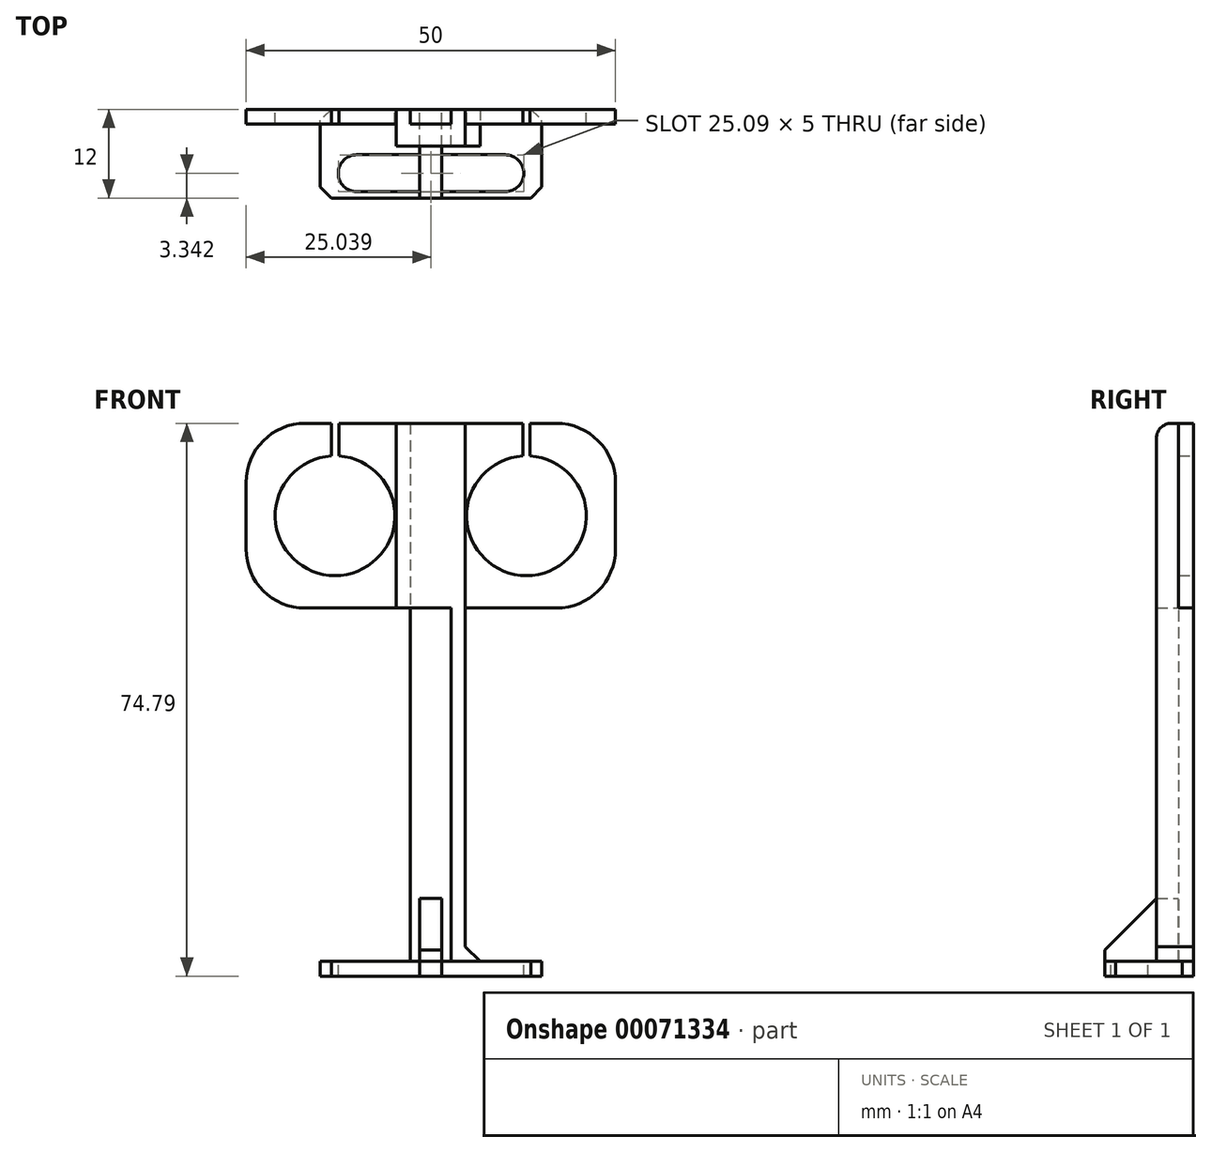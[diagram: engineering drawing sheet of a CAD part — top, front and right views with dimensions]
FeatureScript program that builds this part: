
annotation { "Feature Type Name" : "Feature", "Feature Type Description" : "" }
export const myFeature = defineFeature(function(context is Context, id is Id, definition is map)
    precondition{}
    {
        {
            var Q0;
            Q0=qCreatedBy(makeId("Front.planeOp"),FACE);
            var sketch = newSketch(context, id + "F0", { "sketchPlane" : qUnion([Q0])});
            skLineSegment(sketch, "E0.bottom", {"start": v(25, 38.28) * mm, "end": v(-25, 38.28) * mm});
            skLineSegment(sketch, "E0.top", {"start": v(25, 63.28) * mm, "end": v(-25, 63.28) * mm});
            skLineSegment(sketch, "E0.left", {"start": v(25, 38.28) * mm, "end": v(25, 63.28) * mm});
            skLineSegment(sketch, "E0.right", {"start": v(-25, 38.28) * mm, "end": v(-25, 63.28) * mm});
            skPoint(sketch, "E0.middle", {"position": v(0, 50.78) * mm});
            skCircle(sketch, "E1", {"center": v(-12.95, 50.78) * mm, "radius": 8.1 * mm});
            skCircle(sketch, "E2.MirrorC", {"center": v(12.95, 50.78) * mm, "radius": 8.1 * mm});
            skLineSegment(sketch, "E3", {"start": v(-13.45, 63.28) * mm, "end": v(-13.45, 58.87) * mm});
            skLineSegment(sketch, "E4", {"start": v(-12.95, 50.78) * mm, "end": v(-12.95, 69.58) * mm, "construction": true});
            skLineSegment(sketch, "E5.MirrorCS", {"start": v(-12.45, 63.28) * mm, "end": v(-12.45, 58.87) * mm});
            skLineSegment(sketch, "E6.MirrorCS", {"start": v(12.45, 63.28) * mm, "end": v(12.45, 58.87) * mm});
            skLineSegment(sketch, "E7.MirrorCS", {"start": v(13.45, 63.28) * mm, "end": v(13.45, 58.87) * mm});
            skLineSegment(sketch, "E8", {"start": v(-4.67, 63.28) * mm, "end": v(-4.67, 0) * mm});
            skLineSegment(sketch, "E9", {"start": v(-10.96, -9.5) * mm, "end": v(-15, -9.5) * mm});
            skLineSegment(sketch, "E10", {"start": v(-15, -9.5) * mm, "end": v(-15, -11.5) * mm});
            skLineSegment(sketch, "E11.MirrorCS", {"start": v(10.96, -9.5) * mm, "end": v(15, -9.5) * mm});
            skLineSegment(sketch, "E12.MirrorCS", {"start": v(15, -9.5) * mm, "end": v(15, -11.5) * mm});
            skLineSegment(sketch, "E13", {"start": v(-15, -11.5) * mm, "end": v(15, -11.5) * mm});
            skLineSegment(sketch, "E14", {"start": v(-2.77, 63.28) * mm, "end": v(-2.77, -9.5) * mm});
            skLineSegment(sketch, "E15.MirrorCS", {"start": v(2.77, 63.28) * mm, "end": v(2.77, -9.5) * mm});
            skLineSegment(sketch, "E16", {"start": v(-4.67, 63.28) * mm, "end": v(-4.67, -9.5) * mm});
            skLineSegment(sketch, "E17.MirrorCS", {"start": v(4.67, 63.28) * mm, "end": v(4.67, -9.5) * mm});
            skLineSegment(sketch, "E18", {"start": v(-1.5, -9.5) * mm, "end": v(-1.5, -1) * mm});
            skLineSegment(sketch, "E19.MirrorCS", {"start": v(1.5, -9.5) * mm, "end": v(1.5, -1) * mm});
            skLineSegment(sketch, "E20", {"start": v(-1.5, -1) * mm, "end": v(1.5, -1) * mm});
            skLineSegment(sketch, "E21", {"start": v(-1.5, -9.5) * mm, "end": v(-10.96, -9.5) * mm});
            skLineSegment(sketch, "E22", {"start": v(1.5, -9.5) * mm, "end": v(10.96, -9.5) * mm});
            skLineSegment(sketch, "E23", {"start": v(-1.5, -9.5) * mm, "end": v(-1.5, -11.5) * mm});
            skLineSegment(sketch, "E24", {"start": v(1.5, -9.5) * mm, "end": v(1.5, -11.5) * mm});
            skLineSegment(sketch, "E25.bottom", {"start": v(-4.67, -9.5) * mm, "end": v(-7.17, -9.5) * mm});
            skLineSegment(sketch, "E25.top", {"start": v(-4.67, -7) * mm, "end": v(-7.17, -7) * mm});
            skLineSegment(sketch, "E25.left", {"start": v(-4.67, -9.5) * mm, "end": v(-4.67, -7) * mm});
            skLineSegment(sketch, "E25.right", {"start": v(-7.17, -9.5) * mm, "end": v(-7.17, -7) * mm});
            skPoint(sketch, "E25.middle", {"position": v(-5.92, -8.26) * mm});
            skLineSegment(sketch, "E26", {"start": v(0, 50.78) * mm, "end": v(0, -11.5) * mm, "construction": true});
            skLineSegment(sketch, "E27.MirrorCS", {"start": v(4.67, -7) * mm, "end": v(7.17, -7) * mm});
            skLineSegment(sketch, "E28.MirrorCS", {"start": v(7.17, -9.5) * mm, "end": v(7.17, -7) * mm});
            skSolve(sketch);
        }
        {
            var Q0;
            {var subQ0=sQuery(id+"F0.wireOp",EDGE,"E0.right");Q0=makeQuery(id+"F0.imprint","IMPRINT",FACE,{"disambiguationData":[TD([[makeQuery(id+"F0.imprint","IMPRINT",EDGE,{"derivedFrom":subQ0}),-1.0]])]});}
            var Q1;
            {var subQ0=sQuery(id+"F0.wireOp",EDGE,"E0.left");Q1=makeQuery(id+"F0.imprint","IMPRINT",FACE,{"disambiguationData":[TD([[makeQuery(id+"F0.imprint","IMPRINT",EDGE,{"derivedFrom":subQ0}),1.0]])]});}
            var Q2;
            {var subQ0=sQuery(id+"F0.wireOp",EDGE,"E15.MirrorCS");var subQ1=sQuery(id+"F0.wireOp",EDGE,"E0.bottom");var subQ2=makeQuery(id+"F0.imprint","INTERSECT",VERTEX,{"derivedFrom":[subQ1,subQ0]});Q2=makeQuery(id+"F0.imprint","IMPRINT",FACE,{"disambiguationData":[TD([[makeQuery(id+"F0.imprint","IMPRINT",EDGE,{"disambiguationData":[TD([[subQ2,-1.0]])],"derivedFrom":subQ1}),-1.0]])]});}
            var Q3;
            {var subQ5=sQuery(id+"F0.wireOp",EDGE,"E18");Q3=makeQuery(id+"F0.imprint","IMPRINT",FACE,{"disambiguationData":[TD([[makeQuery(id+"F0.imprint","IMPRINT",EDGE,{"derivedFrom":subQ5}),1.0]])]});}
            extrude(context, id + "F1", {"entities" : qUnion([Q0, Q1, Q2, Q3]), "depth" : 2 * mm});
        }
        {
            var Q0;
            {var subQ0=sQuery(id+"F0.wireOp",EDGE,"E16");var subQ1=sQuery(id+"F0.wireOp",EDGE,"E0.bottom");var subQ2=makeQuery(id+"F0.imprint","INTERSECT",VERTEX,{"derivedFrom":[subQ1,subQ0]});Q0=makeQuery(id+"F0.imprint","IMPRINT",FACE,{"disambiguationData":[TD([[makeQuery(id+"F0.imprint","IMPRINT",EDGE,{"disambiguationData":[TD([[subQ2,1.0]])],"derivedFrom":subQ1}),1.0]])]});}
            var Q1;
            {var subQ0=sQuery(id+"F0.wireOp",EDGE,"E17.MirrorCS");var subQ1=sQuery(id+"F0.wireOp",EDGE,"E0.bottom");var subQ2=makeQuery(id+"F0.imprint","INTERSECT",VERTEX,{"derivedFrom":[subQ1,subQ0]});Q1=makeQuery(id+"F0.imprint","IMPRINT",FACE,{"disambiguationData":[TD([[makeQuery(id+"F0.imprint","IMPRINT",EDGE,{"disambiguationData":[TD([[subQ2,-1.0]])],"derivedFrom":subQ1}),1.0]])]});}
            var Q2;
            {var subQ0=sQuery(id+"F0.wireOp",EDGE,"E17.MirrorCS");var subQ1=sQuery(id+"F0.wireOp",EDGE,"E0.bottom");var subQ2=makeQuery(id+"F0.imprint","INTERSECT",VERTEX,{"derivedFrom":[subQ1,subQ0]});Q2=makeQuery(id+"F0.imprint","IMPRINT",FACE,{"disambiguationData":[TD([[makeQuery(id+"F0.imprint","IMPRINT",EDGE,{"disambiguationData":[TD([[subQ2,-1.0]])],"derivedFrom":subQ1}),-1.0]])]});}
            var Q3;
            {var subQ0=sQuery(id+"F0.wireOp",EDGE,"E16");var subQ1=sQuery(id+"F0.wireOp",EDGE,"E0.bottom");var subQ2=makeQuery(id+"F0.imprint","INTERSECT",VERTEX,{"derivedFrom":[subQ1,subQ0]});Q3=makeQuery(id+"F0.imprint","IMPRINT",FACE,{"disambiguationData":[TD([[makeQuery(id+"F0.imprint","IMPRINT",EDGE,{"disambiguationData":[TD([[subQ2,1.0]])],"derivedFrom":subQ1}),-1.0]])]});}
            var Q4;
            Q4=makeQuery(id+"F0.imprint","IMPRINT",FACE,{"disambiguationData":[TD([[makeQuery(id+"F0.imprint","IMPRINT",EDGE,{"derivedFrom":sQuery(id+"F0.wireOp",EDGE,"E25.bottom")}),-1.0]])]});
            var Q5;
            {var subQ3=sQuery(id+"F0.wireOp",EDGE,"E27.MirrorCS");Q5=makeQuery(id+"F0.imprint","IMPRINT",FACE,{"disambiguationData":[TD([[makeQuery(id+"F0.imprint","IMPRINT",EDGE,{"derivedFrom":subQ3}),-1.0]])]});}
            extrude(context, id + "F2", {"entities" : qUnion([Q0, Q1, Q2, Q3, Q4, Q5]), "depth" : 5 * mm});
        }
        {
            var Q0;
            Q0=makeQuery(id+"F0.imprint","IMPRINT",FACE,{"disambiguationData":[TD([[makeQuery(id+"F0.imprint","IMPRINT",EDGE,{"derivedFrom":sQuery(id+"F0.wireOp",EDGE,"E18")}),-1.0]])]});
            extrude(context, id + "F3", {"entities" : qUnion([Q0]), "operationType" : NewBodyOperationType.ADD, "depth" : 5 * mm});
        }
        {
            var Q0;
            Q0=makeQuery(id+"F3.opExtrude","CAP_FACE",FACE,{"disambiguationData":[OSD([sQuery(id+"F0.wireOp",EDGE,"E13"),sQuery(id+"F0.wireOp",EDGE,"E18"),sQuery(id+"F0.wireOp",EDGE,"E19.MirrorCS"),sQuery(id+"F0.wireOp",EDGE,"E20"),sQuery(id+"F0.wireOp",EDGE,"E23"),sQuery(id+"F0.wireOp",EDGE,"E24")])],"isStart":false});
            extrude(context, id + "F4", {"entities" : qUnion([Q0]), "operationType" : NewBodyOperationType.ADD, "depth" : 7 * mm});
        }
        {
            var Q0;
            Q0=makeQuery(id+"F4.opExtrude","CAP_EDGE",EDGE,{"disambiguationData":[OSD([sQuery(id+"F0.wireOp",EDGE,"E20")])],"isStart":false});
            chamfer(context, id + "F5", {"entities" : qUnion([Q0]), "width" : 7 * mm, "tangentPropagation" : true});
        }
        {
            var Q0;
            {var subQ0=sQuery(id+"F0.wireOp",EDGE,"E0.top");Q0=makeQuery(id+"F1.opExtrude","SWEPT_FACE",FACE,{"disambiguationData":[OSD([subQ0]),TDD([makeQuery(id+"F0.imprint","IMPRINT",EDGE,{"disambiguationData":[TD([[makeQuery(id+"F0.imprint","INTERSECT",VERTEX,{"derivedFrom":[subQ0,sQuery(id+"F0.wireOp",EDGE,"E14")]}),1.0]])],"derivedFrom":subQ0})])]});}
            cPlane(context, id + "F6", {"entities" : qUnion([Q0]), "cplaneType" : CPlaneType.OFFSET, "offset" : 150 * mm, "width" : 150 * mm, "height" : 150 * mm});
        }
        {
            var Q0;
            Q0=makeQuery(id+"F2.opExtrude","SWEPT_FACE",FACE,{"disambiguationData":[OSD([sQuery(id+"F0.wireOp",EDGE,"E22")])]});
            var sketch = newSketch(context, id + "F7", { "sketchPlane" : qUnion([Q0])});
            skLineSegment(sketch, "E29", {"start": v(0.04, 12) * mm, "end": v(-14.96, 12) * mm});
            skLineSegment(sketch, "E30", {"start": v(-14.96, 12) * mm, "end": v(-14.96, 0) * mm});
            skLineSegment(sketch, "E31", {"start": v(0.04, 12) * mm, "end": v(0.04, 6) * mm, "construction": true});
            skLineSegment(sketch, "E32.MirrorCS", {"start": v(15.04, 12) * mm, "end": v(15.04, 0) * mm});
            skLineSegment(sketch, "E33", {"start": v(-14.96, 0) * mm, "end": v(15.04, 0) * mm});
            skLineSegment(sketch, "E34", {"start": v(15.04, 12) * mm, "end": v(0.04, 12) * mm});
            skPoint(sketch, "E35.middle", {"position": v(0.04, 6) * mm});
            skCircle(sketch, "E36", {"center": v(-10, 8.66) * mm, "radius": 2.5 * mm});
            skLineSegment(sketch, "E37", {"start": v(-10, 7.63) * mm, "end": v(-10, 8.66) * mm, "construction": true});
            skCircle(sketch, "E38.MirrorC", {"center": v(10.08, 8.66) * mm, "radius": 2.5 * mm});
            skLineSegment(sketch, "E39", {"start": v(-10, 11.16) * mm, "end": v(10.08, 11.16) * mm});
            skLineSegment(sketch, "E40", {"start": v(-10, 6.16) * mm, "end": v(10.08, 6.16) * mm});
            skSolve(sketch);
        }
        {
            var Q0;
            Q0=makeQuery(id+"F7.imprint","IMPRINT",FACE,{"disambiguationData":[TD([[makeQuery(id+"F7.imprint","IMPRINT",EDGE,{"derivedFrom":sQuery(id+"F7.wireOp",EDGE,"E29")}),1.0]])]});
            var Q1;
            {var subQ0=sQuery(id+"F7.wireOp",EDGE,"E33");var subQ1=sQuery(id+"F0.wireOp",EDGE,"E22");var subQ2=makeQuery(id+"F2.opExtrude","SWEPT_EDGE",EDGE,{"disambiguationData":[OSD([sQuery(id+"F0.wireOp",EDGE,"E15.MirrorCS"),subQ1])]});var subQ3=makeQuery(id+"F7.imprint","INTERSECT",VERTEX,{"derivedFrom":[subQ2,subQ0]});Q1=makeQuery(id+"F7.imprint","IMPRINT",FACE,{"disambiguationData":[TD([[makeQuery(id+"F7.imprint","IMPRINT",EDGE,{"disambiguationData":[TD([[subQ3,-1.0]])],"derivedFrom":subQ0}),1.0]])]});}
            extrude(context, id + "F8", {"entities" : qUnion([Q0, Q1]), "depth" : 2 * mm});
        }
        {
            var Q0;
            Q0=makeQuery(id+"F8.opExtrude","SWEPT_EDGE",EDGE,{"disambiguationData":[OSD([sQuery(id+"F7.wireOp",EDGE,"E32.MirrorCS"),sQuery(id+"F7.wireOp",EDGE,"E34")])]});
            chamfer(context, id + "F9", {"entities" : qUnion([Q0]), "width" : 1.5 * mm, "tangentPropagation" : true});
        }
        {
            var Q0;
            Q0=makeQuery(id+"F8.opExtrude","SWEPT_EDGE",EDGE,{"disambiguationData":[OSD([sQuery(id+"F7.wireOp",EDGE,"E29"),sQuery(id+"F7.wireOp",EDGE,"E30")])]});
            chamfer(context, id + "F10", {"entities" : qUnion([Q0]), "width" : 1.5 * mm, "tangentPropagation" : true});
        }
        {
            var Q0;
            Q0=makeQuery(id+"F8.opExtrude","SWEPT_EDGE",EDGE,{"disambiguationData":[OSD([sQuery(id+"F7.wireOp",EDGE,"E30"),sQuery(id+"F7.wireOp",EDGE,"E33")])]});
            var Q1;
            Q1=makeQuery(id+"F8.opExtrude","SWEPT_EDGE",EDGE,{"disambiguationData":[OSD([sQuery(id+"F7.wireOp",EDGE,"E32.MirrorCS"),sQuery(id+"F7.wireOp",EDGE,"E33")])]});
            chamfer(context, id + "F11", {"entities" : qUnion([Q0, Q1]), "width" : 1.5 * mm, "tangentPropagation" : true});
        }
        {
            var Q0;
            Q0=makeQuery(id+"F1.opExtrude","SWEPT_EDGE",EDGE,{"disambiguationData":[OSD([sQuery(id+"F0.wireOp",EDGE,"E0.bottom"),sQuery(id+"F0.wireOp",EDGE,"E0.left")])]});
            var Q1;
            Q1=makeQuery(id+"F1.opExtrude","SWEPT_EDGE",EDGE,{"disambiguationData":[OSD([sQuery(id+"F0.wireOp",EDGE,"E0.bottom"),sQuery(id+"F0.wireOp",EDGE,"E0.right")])]});
            var Q2;
            Q2=makeQuery(id+"F1.opExtrude","SWEPT_EDGE",EDGE,{"disambiguationData":[OSD([sQuery(id+"F0.wireOp",EDGE,"E0.top"),sQuery(id+"F0.wireOp",EDGE,"E0.right")])]});
            var Q3;
            Q3=makeQuery(id+"F1.opExtrude","SWEPT_EDGE",EDGE,{"disambiguationData":[OSD([sQuery(id+"F0.wireOp",EDGE,"E0.top"),sQuery(id+"F0.wireOp",EDGE,"E0.left")])]});
            fillet(context, id + "F12", {"entities" : qUnion([Q0, Q1, Q2, Q3]), "radius" : 8 * mm, "tangentPropagation" : true, "allowEdgeOverflow" : false});
        }
        {
            var Q0;
            {var subQ0=sQuery(id+"F0.wireOp",EDGE,"E0.top");Q0=makeQuery(id+"F2.opExtrude","CAP_EDGE",EDGE,{"disambiguationData":[OSD([subQ0]),TDD([makeQuery(id+"F0.imprint","IMPRINT",EDGE,{"disambiguationData":[TD([[makeQuery(id+"F0.imprint","INTERSECT",VERTEX,{"derivedFrom":[subQ0,sQuery(id+"F0.wireOp",EDGE,"E15.MirrorCS")]}),1.0]])],"derivedFrom":subQ0})])],"isStart":false});}
            var Q1;
            {var subQ0=sQuery(id+"F0.wireOp",EDGE,"E0.top");Q1=makeQuery(id+"F2.opExtrude","CAP_EDGE",EDGE,{"disambiguationData":[OSD([subQ0]),TDD([makeQuery(id+"F0.imprint","IMPRINT",EDGE,{"disambiguationData":[TD([[makeQuery(id+"F0.imprint","INTERSECT",VERTEX,{"derivedFrom":[subQ0,sQuery(id+"F0.wireOp",EDGE,"E14")]}),-1.0]])],"derivedFrom":subQ0})])],"isStart":false});}
            fillet(context, id + "F13", {"entities" : qUnion([Q0, Q1]), "radius" : 2 * mm, "tangentPropagation" : true, "allowEdgeOverflow" : false});
        }
        {
            var Q0;
            Q0=makeQuery(id+"F2.opExtrude","SWEPT_EDGE",EDGE,{"disambiguationData":[OSD([sQuery(id+"F0.wireOp",EDGE,"E27.MirrorCS"),sQuery(id+"F0.wireOp",EDGE,"E28.MirrorCS")])]});
            var Q1;
            Q1=makeQuery(id+"F2.opExtrude","SWEPT_EDGE",EDGE,{"disambiguationData":[OSD([sQuery(id+"F0.wireOp",EDGE,"E25.top"),sQuery(id+"F0.wireOp",EDGE,"E25.right")])]});
            chamfer(context, id + "F14", {"entities" : qUnion([Q0, Q1]), "width" : 3 * mm, "tangentPropagation" : true});
        }
    });
